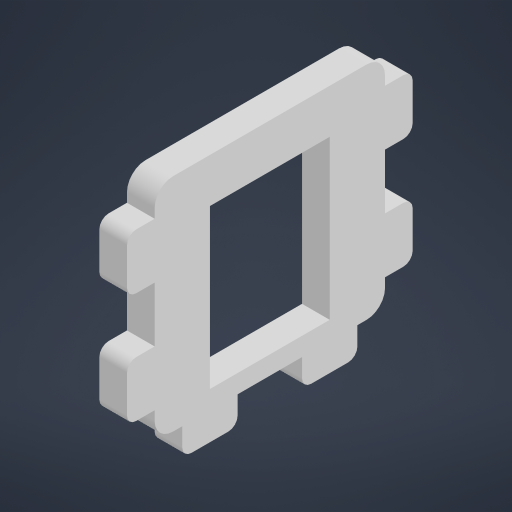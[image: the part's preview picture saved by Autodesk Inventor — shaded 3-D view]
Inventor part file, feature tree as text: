
AUTODESK INVENTOR PART (.ipt)
format: ipt  version: 2023 (Build 270158000, 158)  size: 249,856 bytes
history: native  units: mm
features: extrude x3, sketch x3, fillet x2
ambient origin geometry x8: Origin, YZ Plane, XZ Plane, XY Plane, X Axis, Y Axis, Z Axis, Center Point
bodies: Solid1 (feature_tree)
feature tree (8):
  extrude  "Front Plate"  Depth=25.0mm
  extrude  "Pegs"  TaperAngle=0.0deg  [1 undecoded]
  extrude  "Camera CutOut"  Depth=6.0mm
  fillet  "PiCam Corner Radius"  Radius=3.0mm
  fillet  "Peg Fillet"  Radius=3.0mm
  sketch  "Sketch1"  dims[d0=24.0mm d1=25.0mm]
  sketch  "Sketch2"  dims[d2=3.0mm d3=0.0mm]
  sketch  "Sketch3"  dims[d4=3.0mm d5=6.0mm d6=3.0mm d7=3.0mm d8=6.0mm d9=3.0mm d10=3.0mm d11=0.0mm d12=6.0mm d13=6.0mm d14=4.8mm d15=2.0mm d16=3.0mm d17=0.0mm d18=2.0mm d19=1.0mm]
note: 1 required parameter value undecoded (feature->parameter linkage not recoverable at this tier; creation-order binding heuristic only, values carry confidence <= 0.55)
